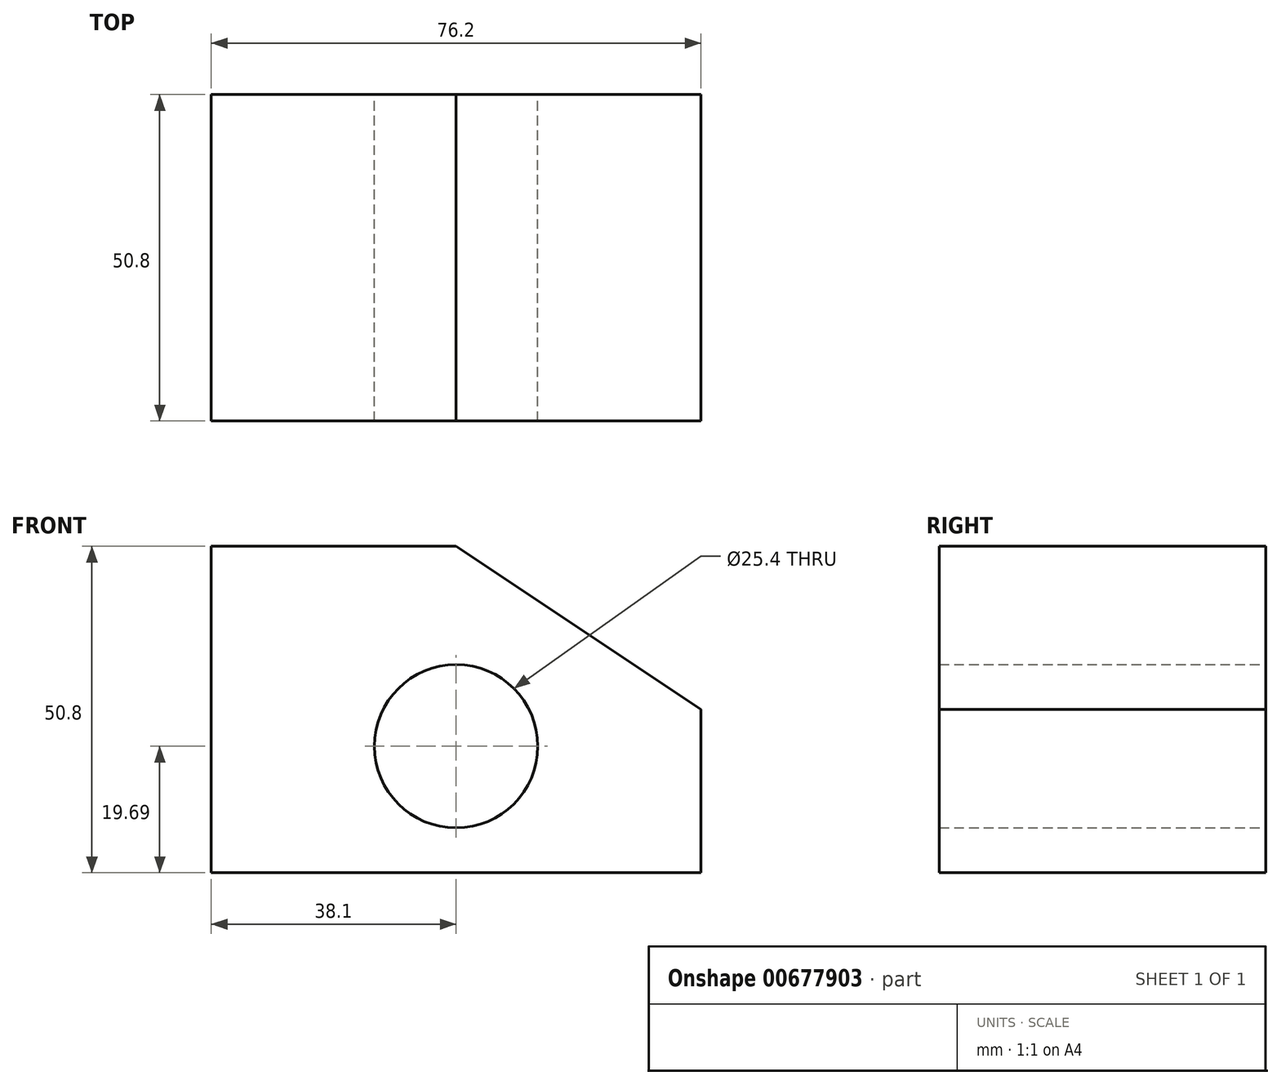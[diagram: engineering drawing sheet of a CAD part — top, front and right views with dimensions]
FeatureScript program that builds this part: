
annotation { "Feature Type Name" : "Feature", "Feature Type Description" : "" }
export const myFeature = defineFeature(function(context is Context, id is Id, definition is map)
    precondition{}
    {
        {
            var Q0;
            Q0=qCreatedBy(makeId("Front.planeOp"),FACE);
            var sketch = newSketch(context, id + "F0", { "sketchPlane" : qUnion([Q0])});
            skLineSegment(sketch, "E0", {"start": v(-38.1, 31.11) * mm, "end": v(-38.1, -19.69) * mm});
            skLineSegment(sketch, "E1", {"start": v(-38.1, -19.69) * mm, "end": v(38.1, -19.69) * mm});
            skLineSegment(sketch, "E2", {"start": v(38.1, -19.69) * mm, "end": v(38.1, 5.71) * mm});
            skLineSegment(sketch, "E3", {"start": v(38.1, 5.71) * mm, "end": v(0, 31.11) * mm});
            skLineSegment(sketch, "E4", {"start": v(0, 31.11) * mm, "end": v(-38.1, 31.11) * mm});
            skCircle(sketch, "E5", {"center": v(0, 0) * mm, "radius": 12.7 * mm});
            skSolve(sketch);
        }
        {
            var Q0;
            Q0=makeQuery(id+"F0.imprint","IMPRINT",FACE,{"disambiguationData":[TD([[makeQuery(id+"F0.imprint","IMPRINT",EDGE,{"derivedFrom":sQuery(id+"F0.wireOp",EDGE,"E0")}),1.0]])]});
            extrude(context, id + "F1", {"entities" : qUnion([Q0]), "depth" : 50.8 * mm, "offsetDistance" : 25.4 * mm});
        }
    });
